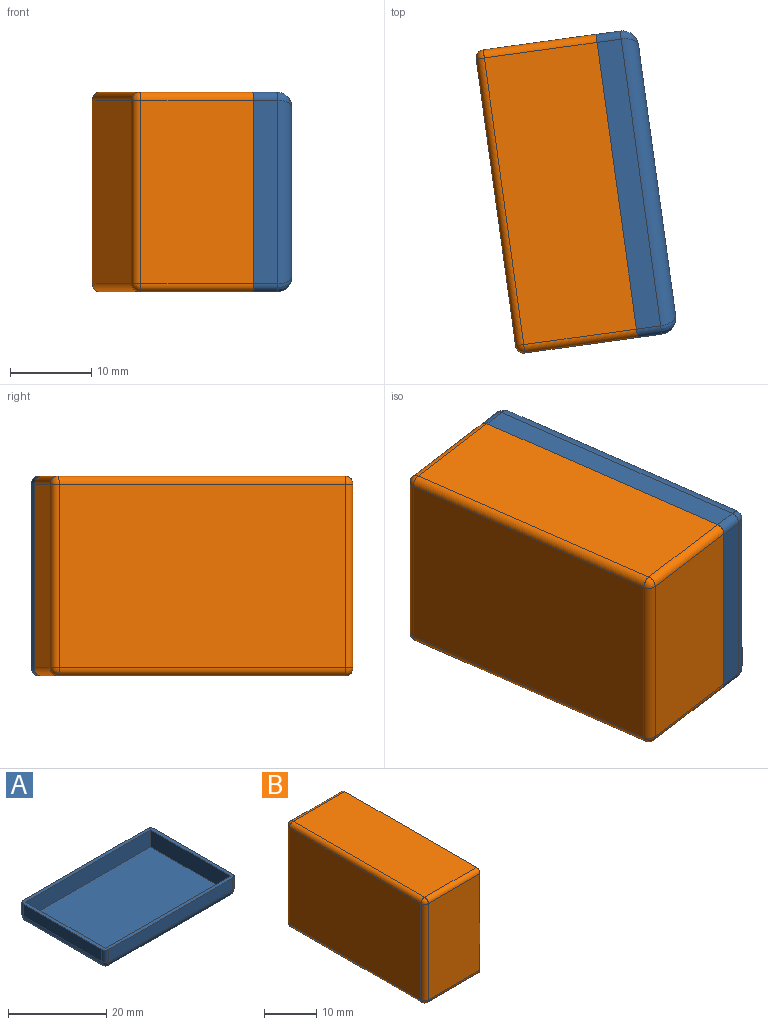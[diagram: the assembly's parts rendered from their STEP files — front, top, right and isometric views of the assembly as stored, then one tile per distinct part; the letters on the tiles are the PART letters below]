
ASSEMBLY  parts=2 mates=1
PART A: 23 faces, bbox 37.6x24.6x5 mm
  f0: plane 37.6x24.6mm, normal (0,0,1), area 96.1mm2, adj f1,f2,f3,f4,f6,f7,f8,f9
  f1: plane 22.6x3mm, normal (1,0,0), area 67.8mm2, adj f0,f11,f14,f16
  f2: plane 35.6x3mm, normal (0,1,0), area 106.8mm2, adj f0,f11,f12,f17
  f3: plane 22.6x3mm, normal (-1,0,0), area 67.8mm2, adj f0,f12,f13,f21
  f4: plane 35.6x3mm, normal (0,-1,0), area 106.8mm2, adj f0,f13,f14,f20
  f5: plane 33.6x20.6mm, normal (0,0,-1), area 692.2mm2, adj f16,f17,f20,f21
  f6: plane 23x4.2mm, normal (-1,0,0), area 96.6mm2, adj f0,f7,f9,f10
  f7: plane 36x4.2mm, normal (0,-1,0), area 151.2mm2, adj f0,f6,f8,f10
  f8: plane 23x4.2mm, normal (1,0,0), area 96.6mm2, adj f0,f7,f9,f10
  f9: plane 36x4.2mm, normal (0,1,0), area 151.2mm2, adj f0,f6,f8,f10
  f10: plane 36x23mm, normal (0,0,1), area 828mm2, adj f6,f7,f8,f9
  f11: cylinder r=1mm len=3mm, axis (0,0,1), area 4.7mm2, adj f0,f1,f2,f15
  f12: cylinder r=1mm len=3mm, axis (0,0,-1), area 4.7mm2, adj f0,f2,f3,f19
  f13: cylinder r=1mm len=3mm, axis (0,0,1), area 4.7mm2, adj f0,f3,f4,f22
  f14: cylinder r=1mm len=3mm, axis (0,0,-1), area 4.7mm2, adj f0,f1,f4,f18
  f15: bspline ~2.39x2mm, area 3.3mm2, adj f11,f16,f17
  f16: cylinder r=2mm len=22.6mm, axis (0,1,0), area 68.7mm2, adj f1,f5,f15,f18
  f17: cylinder r=2mm len=35.6mm, axis (-1,0,0), area 109.6mm2, adj f2,f5,f15,f19
  f18: bspline ~2.39x2mm, area 3.3mm2, adj f14,f16,f20
  f19: bspline ~2.39x2mm, area 3.3mm2, adj f12,f17,f21
  f20: cylinder r=2mm len=35.6mm, axis (1,0,0), area 109.6mm2, adj f4,f5,f18,f22
  f21: cylinder r=2mm len=22.6mm, axis (0,-1,0), area 68.7mm2, adj f3,f5,f19,f22
  f22: bspline ~2.39x2mm, area 3.3mm2, adj f13,f20,f21
PART B: 23 faces, bbox 15x37.6x24.6 mm
  f0: plane 37.6x24.6mm, normal (1,0,0), area 96.1mm2, adj f1,f2,f3,f4,f6,f7,f8,f9
  f1: plane 22.6x14mm, normal (0,1,0), area 316.4mm2, adj f0,f11,f14,f21
  f2: plane 35.6x14mm, normal (0,0,1), area 498.4mm2, adj f0,f11,f12,f20
  f3: plane 22.6x14mm, normal (0,-1,0), area 316.4mm2, adj f0,f12,f13,f16
  f4: plane 35.6x14mm, normal (0,0,-1), area 498.4mm2, adj f0,f13,f14,f17
  f5: plane 35.6x22.6mm, normal (-1,0,0), area 804.6mm2, adj f16,f17,f20,f21
  f6: plane 23x14.2mm, normal (0,-1,0), area 326.6mm2, adj f0,f7,f9,f10
  f7: plane 36x14.2mm, normal (0,0,-1), area 511.2mm2, adj f0,f6,f8,f10
  f8: plane 23x14.2mm, normal (0,1,0), area 326.6mm2, adj f0,f7,f9,f10
  f9: plane 36x14.2mm, normal (0,0,1), area 511.2mm2, adj f0,f6,f8,f10
  f10: plane 36x23mm, normal (1,0,0), area 828mm2, adj f6,f7,f8,f9
  f11: cylinder r=1mm len=14mm, axis (1,0,0), area 22mm2, adj f0,f1,f2,f22
  f12: cylinder r=1mm len=14mm, axis (-1,0,0), area 22mm2, adj f0,f2,f3,f18
  f13: cylinder r=1mm len=14mm, axis (1,0,0), area 22mm2, adj f0,f3,f4,f15
  f14: cylinder r=1mm len=14mm, axis (-1,0,0), area 22mm2, adj f0,f1,f4,f19
  f15: sphere r=1mm, area 1.6mm2, adj f13,f16,f17
  f16: cylinder r=1mm len=22.6mm, axis (0,0,-1), area 35.5mm2, adj f3,f5,f15,f18
  f17: cylinder r=1mm len=35.6mm, axis (0,1,0), area 55.9mm2, adj f4,f5,f15,f19
  f18: sphere r=1mm, area 1.6mm2, adj f12,f16,f20
  f19: sphere r=1mm, area 1.6mm2, adj f14,f17,f21
  f20: cylinder r=1mm len=35.6mm, axis (0,-1,0), area 55.9mm2, adj f2,f5,f18,f22
  f21: cylinder r=1mm len=22.6mm, axis (0,0,1), area 35.5mm2, adj f1,f5,f19,f22
  f22: sphere r=1mm, area 1.6mm2, adj f11,f20,f21
PLACE A rot(axis=(0.63,-0.55,-0.55),115.6deg) t=(5.93,-2.19,-3.74)mm
PLACE B rot(axis=(0,0,1),7.8deg) t=(-13.89,-4.91,-3.74)mm
MATE fastened A.f0 <-> B.f0  axis (-0.99,-0.14,0) through (0.97,-2.87,-3.74)mm
